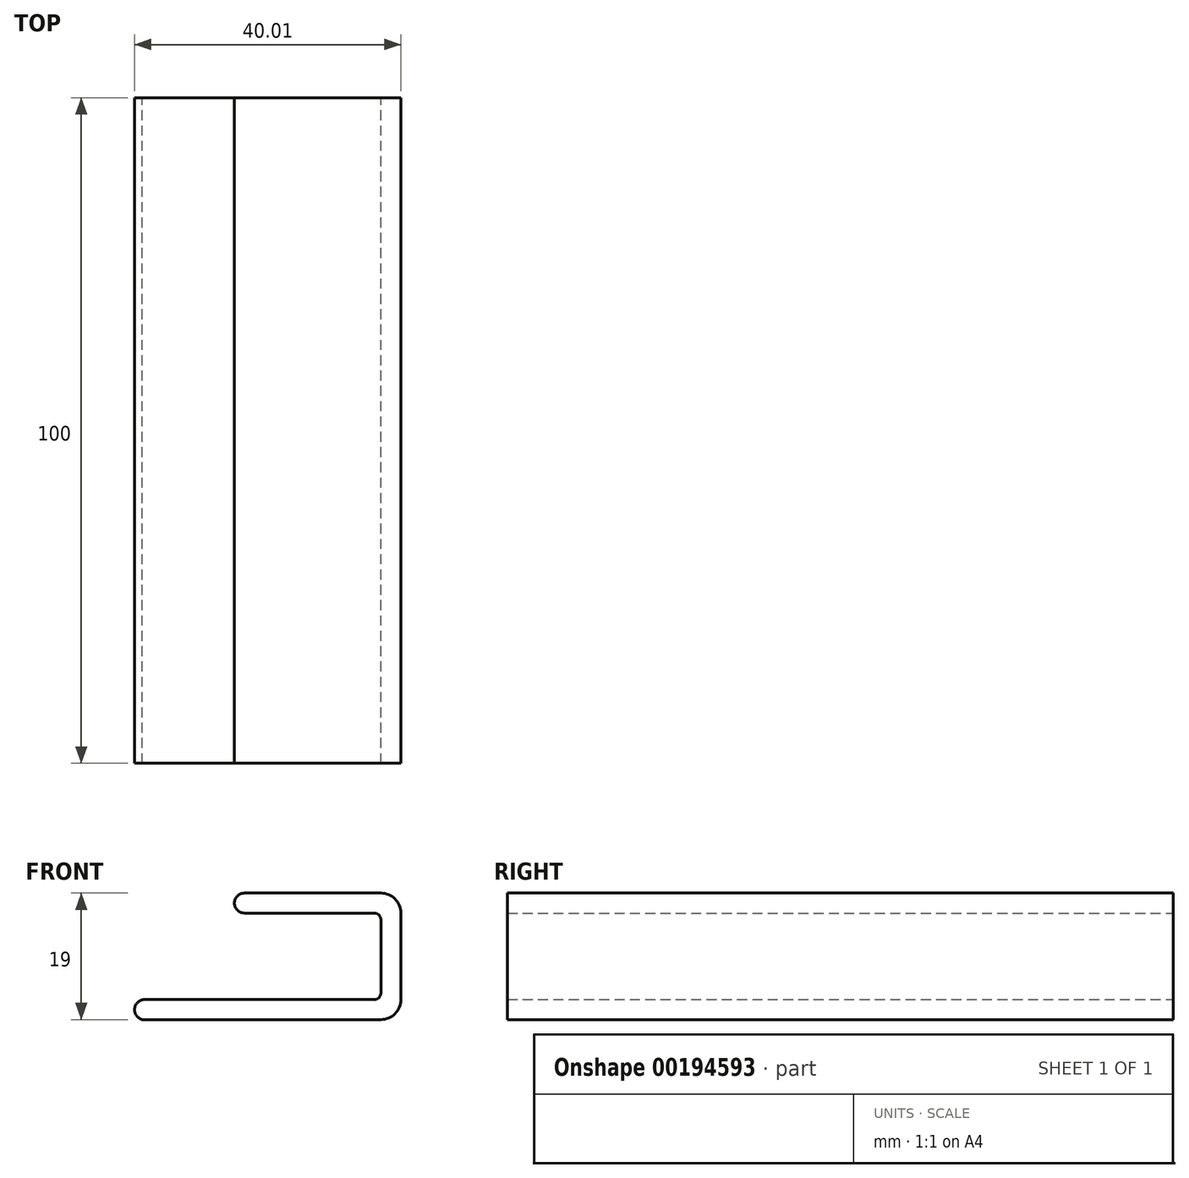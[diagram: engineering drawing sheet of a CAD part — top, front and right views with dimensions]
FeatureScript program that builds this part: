
annotation { "Feature Type Name" : "Feature", "Feature Type Description" : "" }
export const myFeature = defineFeature(function(context is Context, id is Id, definition is map)
    precondition{}
    {
        {
            var Q0;
            Q0=qCreatedBy(makeId("Front.planeOp"),FACE);
            var sketch = newSketch(context, id + "F0", { "sketchPlane" : qUnion([Q0])});
            skLineSegment(sketch, "E0.bottom", {"start": v(21.5, 6.5) * mm, "end": v(2, 6.5) * mm});
            skLineSegment(sketch, "E0.top", {"start": v(21.5, -6.5) * mm, "end": v(-13, -6.5) * mm});
            skLineSegment(sketch, "E0.left", {"start": v(22.5, 5.5) * mm, "end": v(22.5, -5.5) * mm});
            skPoint(sketch, "E0.middle", {"position": v(0, 0) * mm});
            skPoint(sketch, "E1.visualSharp", {"position": v(22.5, 6.5) * mm});
            skArc(sketch, "E1.filletArc", {"start": v(22.5, 5.5) * mm, "mid": v(22.2, 6.2) * mm, "end": v(21.5, 6.5) * mm});
            skPoint(sketch, "E2.visualSharp", {"position": v(22.5, -6.5) * mm});
            skArc(sketch, "E2.filletArc", {"start": v(21.5, -6.5) * mm, "mid": v(22.2, -6.2) * mm, "end": v(22.5, -5.5) * mm});
            skLineSegment(sketch, "E3.0", {"start": v(22.5, 9.5) * mm, "end": v(2, 9.5) * mm});
            skLineSegment(sketch, "E3.1", {"start": v(22.5, -9.5) * mm, "end": v(-13.36, -9.5) * mm});
            skLineSegment(sketch, "E3.3", {"start": v(25.5, 5.5) * mm, "end": v(25.5, -6.5) * mm});
            skLineSegment(sketch, "E4", {"start": v(0.5, 8) * mm, "end": v(0.5, 8) * mm});
            skPoint(sketch, "E0.right.start.orphan", {"position": v(-22.5, 6.5) * mm});
            skPoint(sketch, "E5.visualSharp", {"position": v(0.5, 9.5) * mm});
            skArc(sketch, "E5.filletArc", {"start": v(2, 9.5) * mm, "mid": v(0.94, 9.06) * mm, "end": v(0.5, 8) * mm});
            skPoint(sketch, "E6.visualSharp", {"position": v(0.5, 6.5) * mm});
            skArc(sketch, "E6.filletArc", {"start": v(0.5, 8) * mm, "mid": v(0.94, 6.94) * mm, "end": v(2, 6.5) * mm});
            skPoint(sketch, "E7.visualSharp", {"position": v(-22.5, -6.5) * mm});
            skLineSegment(sketch, "E8", {"start": v(-14.5, -7.96) * mm, "end": v(-14.5, -8) * mm});
            skPoint(sketch, "E9.visualSharp", {"position": v(-14.46, -6.5) * mm});
            skArc(sketch, "E9.filletArc", {"start": v(-13, -6.5) * mm, "mid": v(-14.05, -6.93) * mm, "end": v(-14.5, -7.96) * mm});
            skPoint(sketch, "E10.visualSharp", {"position": v(-14.55, -9.5) * mm});
            skArc(sketch, "E10.filletArc", {"start": v(-14.5, -8) * mm, "mid": v(-14.2, -8.95) * mm, "end": v(-13.36, -9.5) * mm});
            skLineSegment(sketch, "E11", {"start": v(25.5, 5.5) * mm, "end": v(25.5, 6.5) * mm});
            skPoint(sketch, "E12.visualSharp", {"position": v(25.5, 9.5) * mm});
            skArc(sketch, "E12.filletArc", {"start": v(25.5, 6.5) * mm, "mid": v(24.62, 8.62) * mm, "end": v(22.5, 9.5) * mm});
            skArc(sketch, "E13.filletArc", {"start": v(22.5, -9.5) * mm, "mid": v(24.62, -8.62) * mm, "end": v(25.5, -6.5) * mm});
            skSolve(sketch);
        }
        {
            var Q0;
            Q0=makeQuery(id+"F0.imprint","IMPRINT",FACE,{"disambiguationData":[TD([[makeQuery(id+"F0.imprint","IMPRINT",EDGE,{"derivedFrom":sQuery(id+"F0.wireOp",EDGE,"E0.bottom")}),-1.0]])]});
            extrude(context, id + "F1", {"entities" : qUnion([Q0]), "depth" : 100 * mm});
        }
    });
